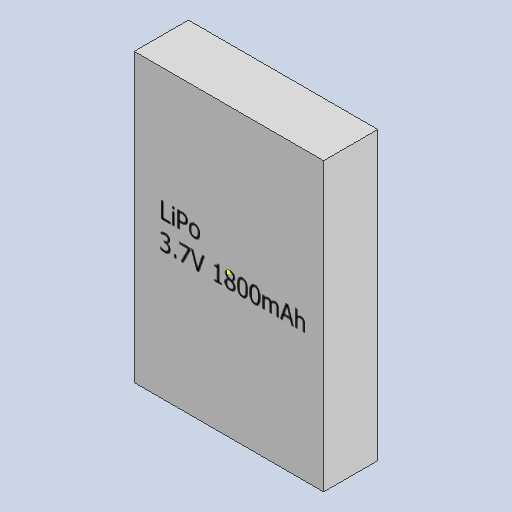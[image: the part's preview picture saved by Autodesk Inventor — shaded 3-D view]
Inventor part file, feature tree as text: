
AUTODESK INVENTOR PART (.ipt)
format: ipt  version: 2025 (Build 290162000, 162)  size: 207,872 bytes
history: native  units: mm
features: sketch x2, other x1, extrude x1
ambient origin geometry x8: Origin, YZ Plane, XZ Plane, XY Plane, X Axis, Y Axis, Z Axis, Center Point
bodies: Body1 (feature_tree)
feature tree (4):
  other  "ソリッド1"
  extrude  "押し出し1"  Depth=35.0mm
  sketch  "スケッチ2"
  sketch  "スケッチ1"
